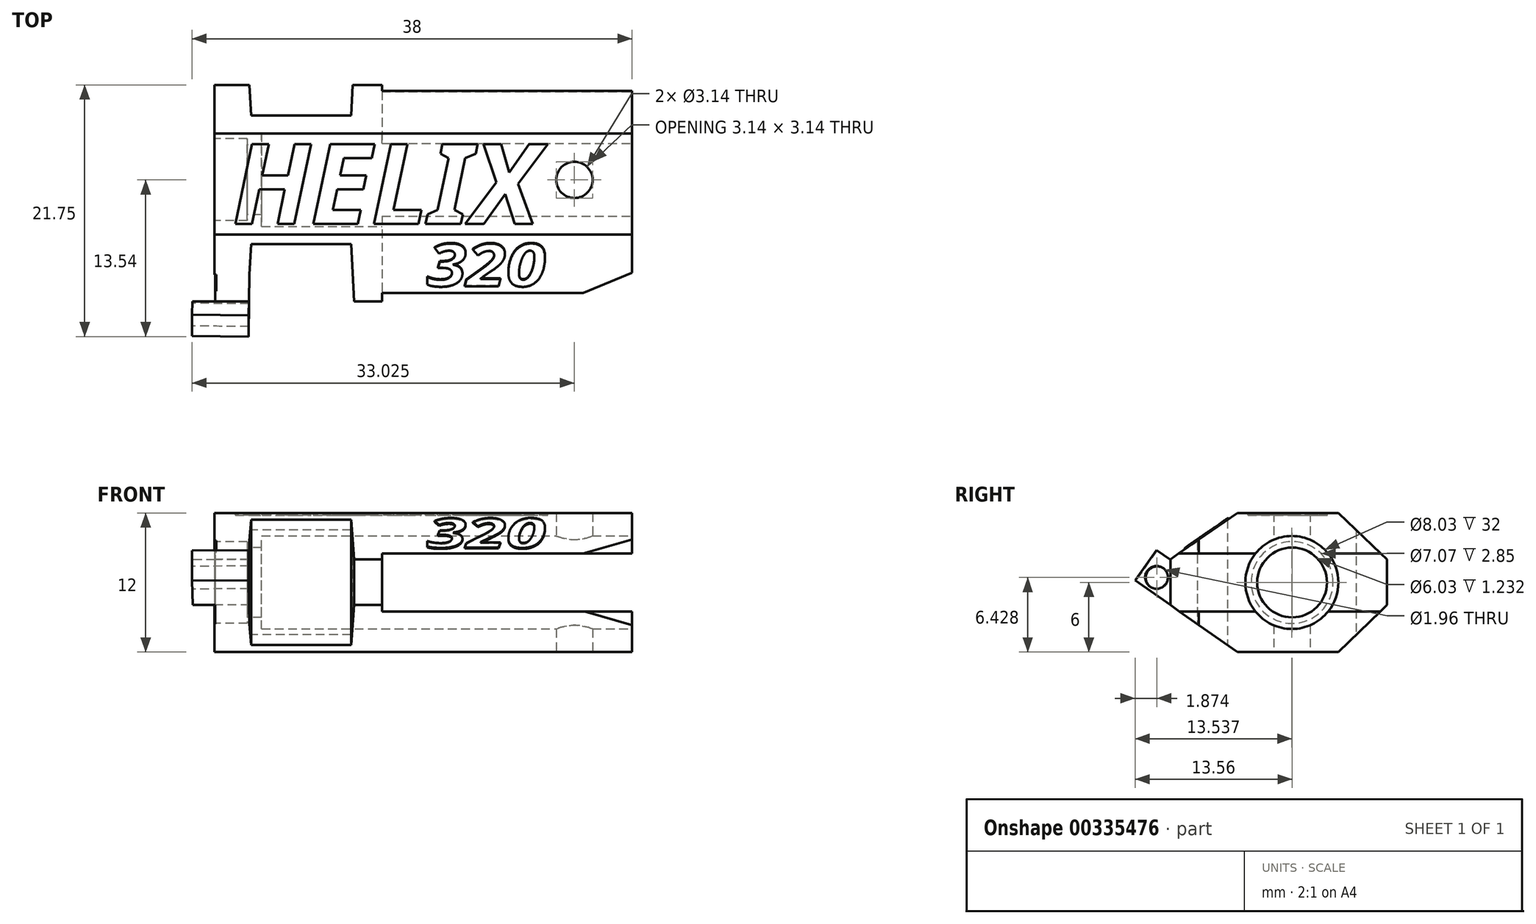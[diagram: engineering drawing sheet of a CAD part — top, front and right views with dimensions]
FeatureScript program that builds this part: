
annotation { "Feature Type Name" : "Feature", "Feature Type Description" : "" }
export const myFeature = defineFeature(function(context is Context, id is Id, definition is map)
    precondition{}
    {
        {
            var Q0;
            Q0=qCreatedBy(makeId("Top.planeOp"),FACE);
            var sketch = newSketch(context, id + "F0", { "sketchPlane" : qUnion([Q0])});
            skLineSegment(sketch, "E0", {"start": v(38, 10.5) * mm, "end": v(38, 18.53) * mm});
            skLineSegment(sketch, "E1", {"start": v(38, 10.5) * mm, "end": v(38, 2.46) * mm});
            skLineSegment(sketch, "E2", {"start": v(38, 18.53) * mm, "end": v(32.02, 21) * mm});
            skLineSegment(sketch, "E3", {"start": v(38, 2.46) * mm, "end": v(32.02, 0) * mm});
            skPoint(sketch, "E4.endSnap0", {"position": v(38, 14.52) * mm});
            skLineSegment(sketch, "E5", {"start": v(32.02, 21) * mm, "end": v(14, 21) * mm});
            skPoint(sketch, "E5.endSnap0", {"position": v(19, 21) * mm});
            skLineSegment(sketch, "E6", {"start": v(32.02, 0) * mm, "end": v(14, 0) * mm});
            skPoint(sketch, "E7.startSnap0", {"position": v(0, 10.5) * mm});
            skLineSegment(sketch, "E8", {"start": v(14, 21) * mm, "end": v(13.74, 16.05) * mm});
            skLineSegment(sketch, "E9", {"start": v(14, 0) * mm, "end": v(13.74, 4.94) * mm});
            skLineSegment(sketch, "E10", {"start": v(13.74, 16.05) * mm, "end": v(5.1, 16.05) * mm});
            skLineSegment(sketch, "E11", {"start": v(13.74, 4.94) * mm, "end": v(5.1, 4.94) * mm});
            skLineSegment(sketch, "E12", {"start": v(5.1, 16.05) * mm, "end": v(4.96, 18.7) * mm});
            skLineSegment(sketch, "E13", {"start": v(5.1, 4.94) * mm, "end": v(4.96, 2.33) * mm});
            skLineSegment(sketch, "E14", {"start": v(4.96, 18.7) * mm, "end": v(1.92, 18.7) * mm});
            skLineSegment(sketch, "E15", {"start": v(1.92, 18.7) * mm, "end": v(1.92, 2.33) * mm});
            skLineSegment(sketch, "E16", {"start": v(1.92, 2.33) * mm, "end": v(0, 2.33) * mm});
            skLineSegment(sketch, "E17", {"start": v(0, 2.33) * mm, "end": v(0, 0) * mm});
            skLineSegment(sketch, "E18", {"start": v(0, 0) * mm, "end": v(4.93, 0) * mm});
            skLineSegment(sketch, "E19", {"start": v(4.93, 0) * mm, "end": v(4.96, 2.33) * mm});
            skCircle(sketch, "E20", {"center": v(33.03, 10.5) * mm, "radius": 1.57 * mm});
            skSolve(sketch);
        }
        {
            var Q0;
            Q0 = qSketchRegion(id + "F0", true);
            extrude(context, id + "F1", {"entities" : qUnion([Q0]), "depth" : 12 * mm});
        }
        {
            var Q0;
            Q0=makeQuery(id+"F1.opExtrude","SWEPT_FACE",FACE,{"disambiguationData":[OSD([sQuery(id+"F0.wireOp",EDGE,"E0"),sQuery(id+"F0.wireOp",EDGE,"E1")])]});
            var sketch = newSketch(context, id + "F2", { "sketchPlane" : qUnion([Q0])});
            skLineSegment(sketch, "E21", {"start": v(2.46, 6) * mm, "end": v(18.53, 6) * mm});
            skCircle(sketch, "E22", {"center": v(10.5, 6) * mm, "radius": 4.01 * mm});
            skSolve(sketch);
        }
        {
            var Q0;
            Q0 = qSketchRegion(id + "F2", true);
            extrude(context, id + "F3", {"entities" : qUnion([Q0]), "operationType" : NewBodyOperationType.REMOVE, "oppositeDirection" : true, "depth" : 32 * mm});
        }
        {
            var Q0;
            Q0=makeQuery(id+"F1.opExtrude","SWEPT_FACE",FACE,{"disambiguationData":[OSD([sQuery(id+"F0.wireOp",EDGE,"E15")])]});
            var sketch = newSketch(context, id + "F4", { "sketchPlane" : qUnion([Q0])});
            skLineSegment(sketch, "E23", {"start": v(-18.7, 6) * mm, "end": v(-2.33, 6) * mm});
            skCircle(sketch, "E24", {"center": v(-10.52, 6) * mm, "radius": 3.54 * mm});
            skSolve(sketch);
        }
        {
            var Q0;
            Q0 = qSketchRegion(id + "F4", true);
            extrude(context, id + "F5", {"entities" : qUnion([Q0]), "operationType" : NewBodyOperationType.REMOVE, "oppositeDirection" : true, "depth" : 2.85 * mm});
        }
        {
            var Q0;
            Q0=makeQuery(id+"F5.boolean.opBoolean","COPY",FACE,{"derivedFrom":makeQuery(id+"F5.opExtrude","CAP_FACE",FACE,{"disambiguationData":[OSD([sQuery(id+"F4.wireOp",EDGE,"E24")])],"isStart":false})});
            var sketch = newSketch(context, id + "F6", { "sketchPlane" : qUnion([Q0])});
            skCircle(sketch, "E25", {"center": v(-10.52, 6) * mm, "radius": 3.01 * mm});
            skSolve(sketch);
        }
        {
            var Q0;
            Q0 = qSketchRegion(id + "F6", true);
            extrude(context, id + "F7", {"entities" : qUnion([Q0]), "operationType" : NewBodyOperationType.REMOVE, "oppositeDirection" : true, "depth" : 0.46 * mm});
        }
        {
            var Q0;
            Q0 = qSketchRegion(id + "F6", true);
            extrude(context, id + "F8", {"entities" : qUnion([Q0]), "operationType" : NewBodyOperationType.REMOVE, "oppositeDirection" : true, "depth" : 25 * mm});
        }
        {
            var Q0;
            Q0=makeQuery(id+"F1.opExtrude","SWEPT_FACE",FACE,{"disambiguationData":[OSD([sQuery(id+"F0.wireOp",EDGE,"E0"),sQuery(id+"F0.wireOp",EDGE,"E1")])]});
            var sketch = newSketch(context, id + "F9", { "sketchPlane" : qUnion([Q0])});
            skLineSegment(sketch, "E26.bottom", {"start": v(23.12, 3.5) * mm, "end": v(-2.12, 3.5) * mm});
            skLineSegment(sketch, "E26.top", {"start": v(23.12, 8.5) * mm, "end": v(-2.12, 8.5) * mm});
            skLineSegment(sketch, "E26.left", {"start": v(23.12, 3.5) * mm, "end": v(23.12, 8.5) * mm});
            skLineSegment(sketch, "E26.right", {"start": v(-2.12, 3.5) * mm, "end": v(-2.12, 8.5) * mm});
            skPoint(sketch, "E26.middle", {"position": v(10.5, 6) * mm});
            skSolve(sketch);
        }
        {
            var Q0;
            Q0 = qSketchRegion(id + "F9", true);
            extrude(context, id + "F10", {"entities" : qUnion([Q0]), "operationType" : NewBodyOperationType.REMOVE, "oppositeDirection" : true, "depth" : 21.6 * mm});
        }
        {
            var Q0;
            Q0=makeQuery(id+"F1.opExtrude","SWEPT_FACE",FACE,{"disambiguationData":[OSD([sQuery(id+"F0.wireOp",EDGE,"E15")])]});
            var sketch = newSketch(context, id + "F11", { "sketchPlane" : qUnion([Q0])});
            skLineSegment(sketch, "E27", {"start": v(-5.78, 12) * mm, "end": v(0, 8) * mm});
            skLineSegment(sketch, "E28", {"start": v(-5.78, 0) * mm, "end": v(0, 4.05) * mm});
            skLineSegment(sketch, "E29", {"start": v(-14.52, 12) * mm, "end": v(-18.7, 8) * mm});
            skLineSegment(sketch, "E30", {"start": v(-14.52, 0) * mm, "end": v(-18.7, 4.05) * mm});
            skLineSegment(sketch, "E31", {"start": v(-14.52, 12) * mm, "end": v(-18.7, 12) * mm});
            skLineSegment(sketch, "E32", {"start": v(-18.7, 12) * mm, "end": v(-18.7, 8) * mm});
            skLineSegment(sketch, "E33", {"start": v(-18.7, 4.05) * mm, "end": v(-18.7, 0) * mm});
            skLineSegment(sketch, "E34", {"start": v(-18.7, 0) * mm, "end": v(-14.52, 0) * mm});
            skLineSegment(sketch, "E35", {"start": v(-5.78, 0) * mm, "end": v(0, -0.5) * mm});
            skLineSegment(sketch, "E36", {"start": v(0, -0.5) * mm, "end": v(0, 4.05) * mm});
            skLineSegment(sketch, "E37", {"start": v(0, 8) * mm, "end": v(0, 12) * mm});
            skLineSegment(sketch, "E38", {"start": v(0, 12) * mm, "end": v(-5.78, 12) * mm});
            skSolve(sketch);
        }
        {
            var Q0;
            Q0 = qSketchRegion(id + "F11", true);
            extrude(context, id + "F12", {"entities" : qUnion([Q0]), "operationType" : NewBodyOperationType.REMOVE, "oppositeDirection" : true, "depth" : 40 * mm});
        }
        {
            var Q0;
            {var subQ0=sQuery(id+"F0.wireOp",EDGE,"E2");var subQ1=sQuery(id+"F0.wireOp",EDGE,"E5");var subQ2=sQuery(id+"F0.wireOp",EDGE,"E8");Q0=makeQuery(id+"F12.boolean.opBoolean","SPLIT",FACE,{"disambiguationData":[TD([makeQuery(id+"F1.opExtrude","SWEPT_FACE",FACE,{"disambiguationData":[OSD([subQ0])]})])],"derivedFrom":makeQuery(id+"F1.opExtrude","CAP_FACE",FACE,{"disambiguationData":[OSD([sQuery(id+"F0.wireOp",EDGE,"E0"),sQuery(id+"F0.wireOp",EDGE,"E1"),subQ0,sQuery(id+"F0.wireOp",EDGE,"E3"),subQ1,sQuery(id+"F0.wireOp",EDGE,"E6"),subQ2,sQuery(id+"F0.wireOp",EDGE,"E9"),sQuery(id+"F0.wireOp",EDGE,"E10"),sQuery(id+"F0.wireOp",EDGE,"E11"),sQuery(id+"F0.wireOp",EDGE,"E12"),sQuery(id+"F0.wireOp",EDGE,"E13"),sQuery(id+"F0.wireOp",EDGE,"E14"),sQuery(id+"F0.wireOp",EDGE,"E15"),sQuery(id+"F0.wireOp",EDGE,"E16"),sQuery(id+"F0.wireOp",EDGE,"E17"),sQuery(id+"F0.wireOp",EDGE,"E18"),sQuery(id+"F0.wireOp",EDGE,"E19"),sQuery(id+"F0.wireOp",EDGE,"E20")])],"isStart":false})});}
            var sketch = newSketch(context, id + "F13", { "sketchPlane" : qUnion([Q0])});
            skLineSegment(sketch, "E39", {"start": v(13.88, 18.7) * mm, "end": v(37.57, 18.7) * mm});
            skLineSegment(sketch, "E40", {"start": v(37.57, 18.7) * mm, "end": v(32.02, 21) * mm});
            skLineSegment(sketch, "E41", {"start": v(32.02, 21) * mm, "end": v(14, 21) * mm});
            skLineSegment(sketch, "E42", {"start": v(14, 21) * mm, "end": v(13.88, 18.7) * mm});
            skSolve(sketch);
        }
        {
            var Q0;
            Q0 = qSketchRegion(id + "F13", true);
            extrude(context, id + "F14", {"entities" : qUnion([Q0]), "operationType" : NewBodyOperationType.REMOVE, "oppositeDirection" : true, "depth" : 25 * mm});
        }
        {
            var Q0;
            Q0=makeQuery(id+"F1.opExtrude","SWEPT_FACE",FACE,{"disambiguationData":[OSD([sQuery(id+"F0.wireOp",EDGE,"E17")])]});
            var sketch = newSketch(context, id + "F15", { "sketchPlane" : qUnion([Q0])});
            skLineSegment(sketch, "E43", {"start": v(-2.33, 12) * mm, "end": v(0, 12) * mm});
            skLineSegment(sketch, "E44", {"start": v(0, 12) * mm, "end": v(0, 8.04) * mm});
            skLineSegment(sketch, "E45", {"start": v(0, 8.04) * mm, "end": v(-2.33, 9.54) * mm});
            skLineSegment(sketch, "E46", {"start": v(-2.33, 9.54) * mm, "end": v(-2.33, 12) * mm});
            skLineSegment(sketch, "E47", {"start": v(0, 3.73) * mm, "end": v(0, 0) * mm});
            skLineSegment(sketch, "E48", {"start": v(0, 0) * mm, "end": v(-2.33, 0) * mm});
            skLineSegment(sketch, "E49", {"start": v(-2.33, 0) * mm, "end": v(-2.33, 2.26) * mm});
            skLineSegment(sketch, "E50", {"start": v(-2.33, 2.26) * mm, "end": v(0, 3.73) * mm});
            skSolve(sketch);
        }
        {
            var Q0;
            Q0 = qSketchRegion(id + "F15", true);
            extrude(context, id + "F16", {"entities" : qUnion([Q0]), "operationType" : NewBodyOperationType.REMOVE, "oppositeDirection" : true, "depth" : 2.1 * mm});
        }
        {
            var Q0;
            Q0=makeQuery(id+"F12.boolean.opBoolean","COPY",FACE,{"derivedFrom":makeQuery(id+"F12.opExtrude","SWEPT_FACE",FACE,{"disambiguationData":[OSD([sQuery(id+"F11.wireOp",EDGE,"E28")])]})});
            var sketch = newSketch(context, id + "F17", { "sketchPlane" : qUnion([Q0])});
            skLineSegment(sketch, "E51", {"start": v(4.93, 2.33) * mm, "end": v(4.88, 6.04) * mm});
            skLineSegment(sketch, "E52", {"start": v(4.88, 6.04) * mm, "end": v(0, 5.98) * mm});
            skLineSegment(sketch, "E53", {"start": v(0, 5.98) * mm, "end": v(0.04, 2.33) * mm});
            skLineSegment(sketch, "E54", {"start": v(0.04, 2.33) * mm, "end": v(4.93, 2.33) * mm});
            skSolve(sketch);
        }
        {
            var Q0;
            Q0 = qSketchRegion(id + "F17", true);
            extrude(context, id + "F18", {"entities" : qUnion([Q0]), "operationType" : NewBodyOperationType.ADD, "oppositeDirection" : true, "depth" : 3.2 * mm});
        }
        {
            var Q0;
            Q0=makeQuery(id+"F1.opExtrude","SWEPT_FACE",FACE,{"disambiguationData":[OSD([sQuery(id+"F0.wireOp",EDGE,"E17")])]});
            var sketch = newSketch(context, id + "F19", { "sketchPlane" : qUnion([Q0])});
            skLineSegment(sketch, "E55", {"start": v(0, 8.04) * mm, "end": v(-2.33, 9.54) * mm});
            skLineSegment(sketch, "E56", {"start": v(-2.33, 9.54) * mm, "end": v(-2.33, 2.26) * mm});
            skLineSegment(sketch, "E57", {"start": v(-2.33, 2.26) * mm, "end": v(0, 3.73) * mm});
            skLineSegment(sketch, "E58", {"start": v(0, 3.73) * mm, "end": v(0, 8.04) * mm});
            skSolve(sketch);
        }
        {
            var Q0;
            Q0 = qSketchRegion(id + "F19", true);
            extrude(context, id + "F20", {"entities" : qUnion([Q0]), "operationType" : NewBodyOperationType.REMOVE, "oppositeDirection" : true, "depth" : 2 * mm});
        }
        {
            var Q0;
            Q0=makeQuery(id+"F18.opExtrude","SWEPT_FACE",FACE,{"disambiguationData":[OSD([sQuery(id+"F17.wireOp",EDGE,"E53")])]});
            var sketch = newSketch(context, id + "F21", { "sketchPlane" : qUnion([Q0])});
            skCircle(sketch, "E59", {"center": v(1.14, 6.41) * mm, "radius": 0.98 * mm});
            skSolve(sketch);
        }
        {
            var Q0;
            Q0 = qSketchRegion(id + "F21", true);
            extrude(context, id + "F22", {"entities" : qUnion([Q0]), "operationType" : NewBodyOperationType.REMOVE, "oppositeDirection" : true, "depth" : 5.8 * mm});
        }
        {
            var Q0;
            {var subQ0=sQuery(id+"F0.wireOp",EDGE,"E20");var subQ1=sQuery(id+"F0.wireOp",EDGE,"E15");var subQ2=sQuery(id+"F0.wireOp",EDGE,"E1");var subQ3=sQuery(id+"F0.wireOp",EDGE,"E0");Q0=makeQuery(id+"F12.boolean.opBoolean","SPLIT",FACE,{"disambiguationData":[TD([makeQuery(id+"F1.opExtrude","SWEPT_FACE",FACE,{"disambiguationData":[OSD([subQ1])]})])],"derivedFrom":makeQuery(id+"F1.opExtrude","CAP_FACE",FACE,{"disambiguationData":[OSD([subQ3,subQ2,sQuery(id+"F0.wireOp",EDGE,"E2"),sQuery(id+"F0.wireOp",EDGE,"E3"),sQuery(id+"F0.wireOp",EDGE,"E5"),sQuery(id+"F0.wireOp",EDGE,"E6"),sQuery(id+"F0.wireOp",EDGE,"E8"),sQuery(id+"F0.wireOp",EDGE,"E9"),sQuery(id+"F0.wireOp",EDGE,"E10"),sQuery(id+"F0.wireOp",EDGE,"E11"),sQuery(id+"F0.wireOp",EDGE,"E12"),sQuery(id+"F0.wireOp",EDGE,"E13"),sQuery(id+"F0.wireOp",EDGE,"E14"),subQ1,sQuery(id+"F0.wireOp",EDGE,"E16"),sQuery(id+"F0.wireOp",EDGE,"E17"),sQuery(id+"F0.wireOp",EDGE,"E18"),sQuery(id+"F0.wireOp",EDGE,"E19"),subQ0])],"isStart":false})});}
            var sketch = newSketch(context, id + "F23", { "sketchPlane" : qUnion([Q0])});
            skText(sketch, "E60", { "text": "HELIX", "fontName": "NotoSans-BoldItalic.ttf"});
            const initialGuessF23  = {"E60": [0.00348, 0.0067, 1, 0, 0.00694]};
            skSetInitialGuess(sketch, initialGuessF23);
            skSolve(sketch);
        }
        {
            var Q0;
            Q0 = qSketchRegion(id + "F23", true);
            extrude(context, id + "F24", {"entities" : qUnion([Q0]), "operationType" : NewBodyOperationType.REMOVE, "oppositeDirection" : true, "depth" : 0.2 * mm});
        }
        {
            var Q0;
            Q0=makeQuery(id+"F12.boolean.opBoolean","COPY",FACE,{"derivedFrom":makeQuery(id+"F12.opExtrude","SWEPT_FACE",FACE,{"disambiguationData":[OSD([sQuery(id+"F11.wireOp",EDGE,"E27")])]})});
            var sketch = newSketch(context, id + "F25", { "sketchPlane" : qUnion([Q0])});
            skText(sketch, "E61", { "text": "320", "fontName": "NotoSans-BoldItalic.ttf"});
            const initialGuessF25  = {"E61": [0.02028, 0.0062, 1, 0, 0.00447]};
            skSetInitialGuess(sketch, initialGuessF25);
            skSolve(sketch);
        }
        {
            var Q0;
            Q0 = qSketchRegion(id + "F25", true);
            extrude(context, id + "F26", {"entities" : qUnion([Q0]), "operationType" : NewBodyOperationType.ADD, "depth" : 0.1 * mm});
        }
    });
